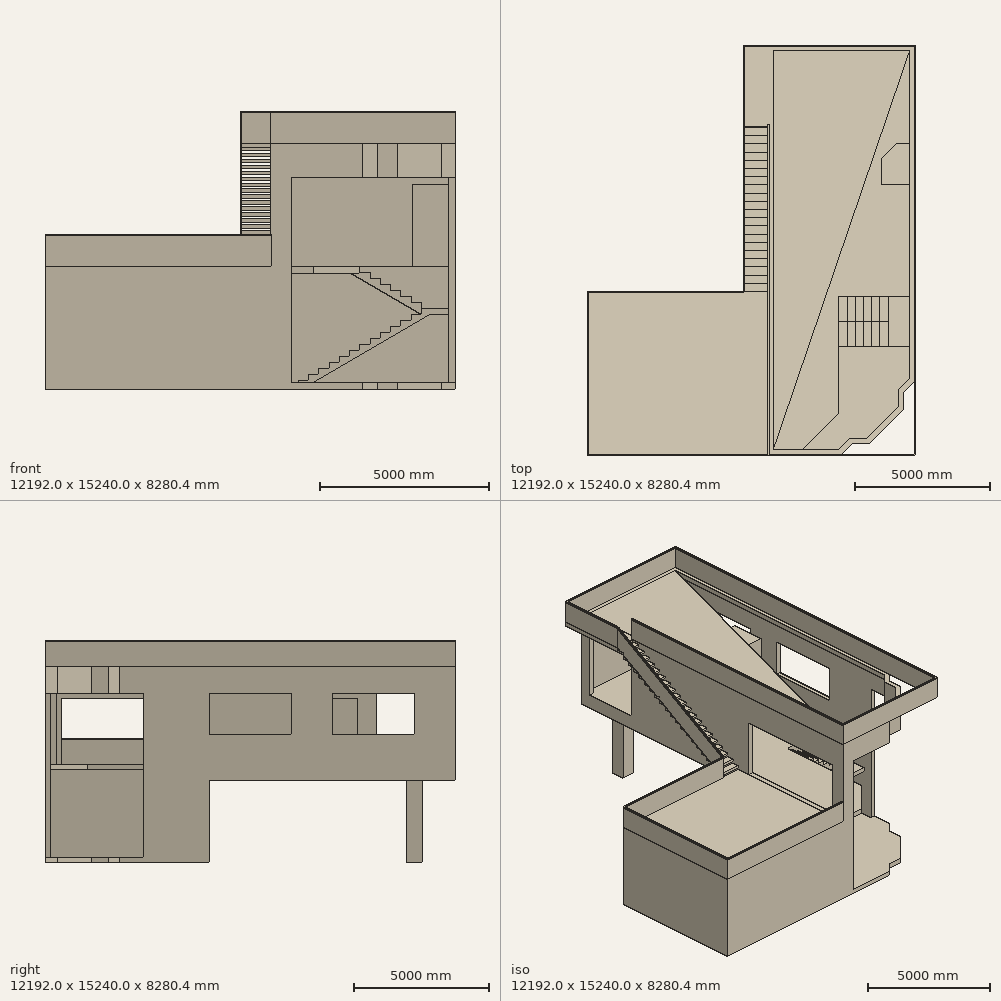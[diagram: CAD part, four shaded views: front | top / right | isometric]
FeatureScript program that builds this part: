
annotation { "Feature Type Name" : "Feature", "Feature Type Description" : "" }
export const myFeature = defineFeature(function(context is Context, id is Id, definition is map)
    precondition{}
    {
        {
            var Q0;
            Q0=qCreatedBy(makeId("Top.planeOp"),FACE);
            var sketch = newSketch(context, id + "F0", { "sketchPlane" : qUnion([Q0])});
            skLineSegment(sketch, "E0.bottom", {"start": v(0, 6096) * mm, "end": v(-12192, 6096) * mm});
            skLineSegment(sketch, "E0.top", {"start": v(0, 0) * mm, "end": v(-12192, 0) * mm});
            skLineSegment(sketch, "E0.left", {"start": v(0, 6096) * mm, "end": v(0, 0) * mm});
            skLineSegment(sketch, "E0.right", {"start": v(-12192, 6096) * mm, "end": v(-12192, 0) * mm});
            skSolve(sketch);
        }
        {
            var Q0;
            Q0 = qSketchRegion(id + "F0", true);
            extrude(context, id + "F1", {"entities" : qUnion([Q0]), "depth" : 3657.6 * mm, "offsetDistance" : 25.4 * mm});
        }
        {
            var Q0;
            Q0=makeQuery(id+"F1.opExtrude","CAP_FACE",FACE,{"disambiguationData":[OSD([sQuery(id+"F0.wireOp",EDGE,"E0.bottom"),sQuery(id+"F0.wireOp",EDGE,"E0.top"),sQuery(id+"F0.wireOp",EDGE,"E0.left"),sQuery(id+"F0.wireOp",EDGE,"E0.right")])],"isStart":false});
            var sketch = newSketch(context, id + "F2", { "sketchPlane" : qUnion([Q0])});
            skLineSegment(sketch, "E1", {"start": v(0, 6096) * mm, "end": v(0, 15240) * mm});
            skLineSegment(sketch, "E2", {"start": v(0, 15240) * mm, "end": v(-5486.4, 15240) * mm});
            skLineSegment(sketch, "E3", {"start": v(-5486.4, 15240) * mm, "end": v(-5486.4, 0) * mm});
            skLineSegment(sketch, "E4", {"start": v(-5486.4, 0) * mm, "end": v(0, 0) * mm});
            skLineSegment(sketch, "E5", {"start": v(0, 0) * mm, "end": v(0, 6096) * mm});
            skSolve(sketch);
        }
        {
            var Q0;
            {var subQ0=sQuery(id+"F2.wireOp",EDGE,"E1");Q0=makeQuery(id+"F2.imprint","IMPRINT",FACE,{"disambiguationData":[TD([[makeQuery(id+"F2.imprint","IMPRINT",EDGE,{"derivedFrom":subQ0}),1.0]])]});}
            var Q1;
            {var subQ0=sQuery(id+"F2.wireOp",EDGE,"E4");Q1=makeQuery(id+"F2.imprint","IMPRINT",FACE,{"disambiguationData":[TD([[makeQuery(id+"F2.imprint","IMPRINT",EDGE,{"derivedFrom":subQ0}),-1.0]])]});}
            extrude(context, id + "F3", {"entities" : qUnion([Q0, Q1]), "operationType" : NewBodyOperationType.ADD, "depth" : 3657.6 * mm, "offsetDistance" : 25.4 * mm});
        }
        {
            var Q0;
            Q0=makeQuery(id+"F3.opExtrude","SWEPT_FACE",FACE,{"disambiguationData":[OSD([sQuery(id+"F2.wireOp",EDGE,"E3")])]});
            var sketch = newSketch(context, id + "F4", { "sketchPlane" : qUnion([Q0])});
            skLineSegment(sketch, "E6.bottom", {"start": v(-6096, 3835.4) * mm, "end": v(-6400.8, 3835.4) * mm});
            skLineSegment(sketch, "E6.top", {"start": v(-6096, 3733.8) * mm, "end": v(-6400.8, 3733.8) * mm});
            skLineSegment(sketch, "E6.left", {"start": v(-6096, 3835.4) * mm, "end": v(-6096, 3733.8) * mm});
            skLineSegment(sketch, "E7", {"start": v(-6400.8, 3835.4) * mm, "end": v(-6400.8, 3733.8) * mm});
            skLineSegment(sketch, "E8", {"start": v(-6096, 3657.6) * mm, "end": v(-6096, 3733.8) * mm, "construction": true});
            skLineSegment(sketch, "E9", {"start": v(-6400.8, 3835.4) * mm, "end": v(-6096, 3657.6) * mm, "construction": true});
            skLineSegment(sketch, "E10", {"start": v(-6400.8, 3835.4) * mm, "end": v(-6705.6, 4013.2) * mm, "construction": true});
            skLineSegment(sketch, "E11.0.1.0", {"start": v(-6400.8, 4013.2) * mm, "end": v(-6705.6, 4013.2) * mm});
            skLineSegment(sketch, "E11.0.1.1", {"start": v(-6400.8, 3911.6) * mm, "end": v(-6705.6, 3911.6) * mm});
            skLineSegment(sketch, "E11.0.1.2", {"start": v(-6705.6, 4013.2) * mm, "end": v(-6705.6, 3911.6) * mm});
            skLineSegment(sketch, "E11.0.1.3", {"start": v(-6400.8, 4013.2) * mm, "end": v(-6400.8, 3911.6) * mm});
            skLineSegment(sketch, "E11.0.2.0", {"start": v(-6705.6, 4191) * mm, "end": v(-7010.4, 4191) * mm});
            skLineSegment(sketch, "E11.0.2.1", {"start": v(-6705.6, 4089.4) * mm, "end": v(-7010.4, 4089.4) * mm});
            skLineSegment(sketch, "E11.0.2.2", {"start": v(-7010.4, 4191) * mm, "end": v(-7010.4, 4089.4) * mm});
            skLineSegment(sketch, "E11.0.2.3", {"start": v(-6705.6, 4191) * mm, "end": v(-6705.6, 4089.4) * mm});
            skLineSegment(sketch, "E11.0.3.0", {"start": v(-7010.4, 4368.8) * mm, "end": v(-7315.2, 4368.8) * mm});
            skLineSegment(sketch, "E11.0.3.1", {"start": v(-7010.4, 4267.2) * mm, "end": v(-7315.2, 4267.2) * mm});
            skLineSegment(sketch, "E11.0.3.2", {"start": v(-7315.2, 4368.8) * mm, "end": v(-7315.2, 4267.2) * mm});
            skLineSegment(sketch, "E11.0.3.3", {"start": v(-7010.4, 4368.8) * mm, "end": v(-7010.4, 4267.2) * mm});
            skLineSegment(sketch, "E11.0.4.0", {"start": v(-7315.2, 4546.6) * mm, "end": v(-7620, 4546.6) * mm});
            skLineSegment(sketch, "E11.0.4.1", {"start": v(-7315.2, 4445) * mm, "end": v(-7620, 4445) * mm});
            skLineSegment(sketch, "E11.0.4.2", {"start": v(-7620, 4546.6) * mm, "end": v(-7620, 4445) * mm});
            skLineSegment(sketch, "E11.0.4.3", {"start": v(-7315.2, 4546.6) * mm, "end": v(-7315.2, 4445) * mm});
            skLineSegment(sketch, "E11.0.5.0", {"start": v(-7620, 4724.4) * mm, "end": v(-7924.8, 4724.4) * mm});
            skLineSegment(sketch, "E11.0.5.1", {"start": v(-7620, 4622.8) * mm, "end": v(-7924.8, 4622.8) * mm});
            skLineSegment(sketch, "E11.0.5.2", {"start": v(-7924.8, 4724.4) * mm, "end": v(-7924.8, 4622.8) * mm});
            skLineSegment(sketch, "E11.0.5.3", {"start": v(-7620, 4724.4) * mm, "end": v(-7620, 4622.8) * mm});
            skLineSegment(sketch, "E11.0.6.0", {"start": v(-7924.8, 4902.2) * mm, "end": v(-8229.6, 4902.2) * mm});
            skLineSegment(sketch, "E11.0.6.1", {"start": v(-7924.8, 4800.6) * mm, "end": v(-8229.6, 4800.6) * mm});
            skLineSegment(sketch, "E11.0.6.2", {"start": v(-8229.6, 4902.2) * mm, "end": v(-8229.6, 4800.6) * mm});
            skLineSegment(sketch, "E11.0.6.3", {"start": v(-7924.8, 4902.2) * mm, "end": v(-7924.8, 4800.6) * mm});
            skLineSegment(sketch, "E11.0.7.0", {"start": v(-8229.6, 5080) * mm, "end": v(-8534.4, 5080) * mm});
            skLineSegment(sketch, "E11.0.7.1", {"start": v(-8229.6, 4978.4) * mm, "end": v(-8534.4, 4978.4) * mm});
            skLineSegment(sketch, "E11.0.7.2", {"start": v(-8534.4, 5080) * mm, "end": v(-8534.4, 4978.4) * mm});
            skLineSegment(sketch, "E11.0.7.3", {"start": v(-8229.6, 5080) * mm, "end": v(-8229.6, 4978.4) * mm});
            skLineSegment(sketch, "E11.0.8.0", {"start": v(-8534.4, 5257.8) * mm, "end": v(-8839.2, 5257.8) * mm});
            skLineSegment(sketch, "E11.0.8.1", {"start": v(-8534.4, 5156.2) * mm, "end": v(-8839.2, 5156.2) * mm});
            skLineSegment(sketch, "E11.0.8.2", {"start": v(-8839.2, 5257.8) * mm, "end": v(-8839.2, 5156.2) * mm});
            skLineSegment(sketch, "E11.0.8.3", {"start": v(-8534.4, 5257.8) * mm, "end": v(-8534.4, 5156.2) * mm});
            skLineSegment(sketch, "E11.0.9.0", {"start": v(-8839.2, 5435.6) * mm, "end": v(-9144, 5435.6) * mm});
            skLineSegment(sketch, "E11.0.9.1", {"start": v(-8839.2, 5334) * mm, "end": v(-9144, 5334) * mm});
            skLineSegment(sketch, "E11.0.9.2", {"start": v(-9144, 5435.6) * mm, "end": v(-9144, 5334) * mm});
            skLineSegment(sketch, "E11.0.9.3", {"start": v(-8839.2, 5435.6) * mm, "end": v(-8839.2, 5334) * mm});
            skLineSegment(sketch, "E11.0.10.0", {"start": v(-9144, 5613.4) * mm, "end": v(-9448.8, 5613.4) * mm});
            skLineSegment(sketch, "E11.0.10.1", {"start": v(-9144, 5511.8) * mm, "end": v(-9448.8, 5511.8) * mm});
            skLineSegment(sketch, "E11.0.10.2", {"start": v(-9448.8, 5613.4) * mm, "end": v(-9448.8, 5511.8) * mm});
            skLineSegment(sketch, "E11.0.10.3", {"start": v(-9144, 5613.4) * mm, "end": v(-9144, 5511.8) * mm});
            skLineSegment(sketch, "E11.0.11.0", {"start": v(-9448.8, 5791.2) * mm, "end": v(-9753.6, 5791.2) * mm});
            skLineSegment(sketch, "E11.0.11.1", {"start": v(-9448.8, 5689.6) * mm, "end": v(-9753.6, 5689.6) * mm});
            skLineSegment(sketch, "E11.0.11.2", {"start": v(-9753.6, 5791.2) * mm, "end": v(-9753.6, 5689.6) * mm});
            skLineSegment(sketch, "E11.0.11.3", {"start": v(-9448.8, 5791.2) * mm, "end": v(-9448.8, 5689.6) * mm});
            skLineSegment(sketch, "E11.0.12.0", {"start": v(-9753.6, 5969) * mm, "end": v(-10058.4, 5969) * mm});
            skLineSegment(sketch, "E11.0.12.1", {"start": v(-9753.6, 5867.4) * mm, "end": v(-10058.4, 5867.4) * mm});
            skLineSegment(sketch, "E11.0.12.2", {"start": v(-10058.4, 5969) * mm, "end": v(-10058.4, 5867.4) * mm});
            skLineSegment(sketch, "E11.0.12.3", {"start": v(-9753.6, 5969) * mm, "end": v(-9753.6, 5867.4) * mm});
            skLineSegment(sketch, "E11.0.13.0", {"start": v(-10058.4, 6146.8) * mm, "end": v(-10363.2, 6146.8) * mm});
            skLineSegment(sketch, "E11.0.13.1", {"start": v(-10058.4, 6045.2) * mm, "end": v(-10363.2, 6045.2) * mm});
            skLineSegment(sketch, "E11.0.13.2", {"start": v(-10363.2, 6146.8) * mm, "end": v(-10363.2, 6045.2) * mm});
            skLineSegment(sketch, "E11.0.13.3", {"start": v(-10058.4, 6146.8) * mm, "end": v(-10058.4, 6045.2) * mm});
            skLineSegment(sketch, "E11.0.14.0", {"start": v(-10363.2, 6324.6) * mm, "end": v(-10668, 6324.6) * mm});
            skLineSegment(sketch, "E11.0.14.1", {"start": v(-10363.2, 6223) * mm, "end": v(-10668, 6223) * mm});
            skLineSegment(sketch, "E11.0.14.2", {"start": v(-10668, 6324.6) * mm, "end": v(-10668, 6223) * mm});
            skLineSegment(sketch, "E11.0.14.3", {"start": v(-10363.2, 6324.6) * mm, "end": v(-10363.2, 6223) * mm});
            skLineSegment(sketch, "E11.0.15.0", {"start": v(-10668, 6502.4) * mm, "end": v(-10972.8, 6502.4) * mm});
            skLineSegment(sketch, "E11.0.15.1", {"start": v(-10668, 6400.8) * mm, "end": v(-10972.8, 6400.8) * mm});
            skLineSegment(sketch, "E11.0.15.2", {"start": v(-10972.8, 6502.4) * mm, "end": v(-10972.8, 6400.8) * mm});
            skLineSegment(sketch, "E11.0.15.3", {"start": v(-10668, 6502.4) * mm, "end": v(-10668, 6400.8) * mm});
            skLineSegment(sketch, "E11.0.16.0", {"start": v(-10972.8, 6680.2) * mm, "end": v(-11277.6, 6680.2) * mm});
            skLineSegment(sketch, "E11.0.16.1", {"start": v(-10972.8, 6578.6) * mm, "end": v(-11277.6, 6578.6) * mm});
            skLineSegment(sketch, "E11.0.16.2", {"start": v(-11277.6, 6680.2) * mm, "end": v(-11277.6, 6578.6) * mm});
            skLineSegment(sketch, "E11.0.16.3", {"start": v(-10972.8, 6680.2) * mm, "end": v(-10972.8, 6578.6) * mm});
            skLineSegment(sketch, "E11.0.17.0", {"start": v(-11277.6, 6858) * mm, "end": v(-11582.4, 6858) * mm});
            skLineSegment(sketch, "E11.0.17.1", {"start": v(-11277.6, 6756.4) * mm, "end": v(-11582.4, 6756.4) * mm});
            skLineSegment(sketch, "E11.0.17.2", {"start": v(-11582.4, 6858) * mm, "end": v(-11582.4, 6756.4) * mm});
            skLineSegment(sketch, "E11.0.17.3", {"start": v(-11277.6, 6858) * mm, "end": v(-11277.6, 6756.4) * mm});
            skLineSegment(sketch, "E11.0.18.0", {"start": v(-11582.4, 7035.8) * mm, "end": v(-11887.2, 7035.8) * mm});
            skLineSegment(sketch, "E11.0.18.1", {"start": v(-11582.4, 6934.2) * mm, "end": v(-11887.2, 6934.2) * mm});
            skLineSegment(sketch, "E11.0.18.2", {"start": v(-11887.2, 7035.8) * mm, "end": v(-11887.2, 6934.2) * mm});
            skLineSegment(sketch, "E11.0.18.3", {"start": v(-11582.4, 7035.8) * mm, "end": v(-11582.4, 6934.2) * mm});
            skLineSegment(sketch, "E11.0.19.0", {"start": v(-11887.2, 7213.6) * mm, "end": v(-12192, 7213.6) * mm});
            skLineSegment(sketch, "E11.0.19.1", {"start": v(-11887.2, 7112) * mm, "end": v(-12192, 7112) * mm});
            skLineSegment(sketch, "E11.0.19.2", {"start": v(-12192, 7213.6) * mm, "end": v(-12192, 7112) * mm});
            skLineSegment(sketch, "E11.0.19.3", {"start": v(-11887.2, 7213.6) * mm, "end": v(-11887.2, 7112) * mm});
            skLineSegment(sketch, "E11.direction1", {"start": v(-6400.8, 3733.8) * mm, "end": v(-6375.4, 3733.8) * mm, "construction": true});
            skLineSegment(sketch, "E11.direction2", {"start": v(-6400.8, 3733.8) * mm, "end": v(-6705.6, 3911.6) * mm, "construction": true});
            skLineSegment(sketch, "E12", {"start": v(-15240, 7112) * mm, "end": v(-15240, 7315.2) * mm});
            skLineSegment(sketch, "E13", {"start": v(-12242.8, 7315.2) * mm, "end": v(-12242.8, 7112) * mm});
            skLineSegment(sketch, "E14", {"start": v(-12242.8, 7112) * mm, "end": v(-15240, 7112) * mm});
            skLineSegment(sketch, "E15", {"start": v(-15240, 7315.2) * mm, "end": v(-12242.8, 7315.2) * mm});
            skSolve(sketch);
        }
        {
            var Q0;
            Q0 = qSketchRegion(id + "F4", true);
            extrude(context, id + "F5", {"entities" : qUnion([Q0]), "operationType" : NewBodyOperationType.ADD, "depth" : 914.4 * mm, "offsetDistance" : 25.4 * mm});
        }
        {
            var Q0;
            Q0=makeQuery(id+"F1.opExtrude","CAP_FACE",FACE,{"disambiguationData":[OSD([sQuery(id+"F0.wireOp",EDGE,"E0.bottom"),sQuery(id+"F0.wireOp",EDGE,"E0.top"),sQuery(id+"F0.wireOp",EDGE,"E0.left"),sQuery(id+"F0.wireOp",EDGE,"E0.right")])],"isStart":false});
            var sketch = newSketch(context, id + "F6", { "sketchPlane" : qUnion([Q0])});
            skLineSegment(sketch, "E16.0", {"start": v(-5486.4, 50.8) * mm, "end": v(-12141.2, 50.8) * mm});
            skLineSegment(sketch, "E16.1", {"start": v(-12141.2, 6045.2) * mm, "end": v(-12141.2, 50.8) * mm});
            skLineSegment(sketch, "E16.2", {"start": v(-6400.8, 6045.2) * mm, "end": v(-12141.2, 6045.2) * mm});
            skLineSegment(sketch, "E17", {"start": v(-5486.4, 50.8) * mm, "end": v(-5486.4, 0) * mm});
            skLineSegment(sketch, "E18", {"start": v(-5486.4, 0) * mm, "end": v(-12192, 0) * mm});
            skLineSegment(sketch, "E19", {"start": v(-12192, 0) * mm, "end": v(-12192, 6096) * mm});
            skLineSegment(sketch, "E20", {"start": v(-12192, 6096) * mm, "end": v(-6400.8, 6096) * mm});
            skLineSegment(sketch, "E21", {"start": v(-6400.8, 6096) * mm, "end": v(-6400.8, 6045.2) * mm});
            skSolve(sketch);
        }
        {
            var Q0;
            Q0=makeQuery(id+"F6.imprint","IMPRINT",FACE,{"disambiguationData":[TD([[makeQuery(id+"F6.imprint","IMPRINT",EDGE,{"derivedFrom":sQuery(id+"F6.wireOp",EDGE,"E16.0")}),1.0]])]});
            extrude(context, id + "F7", {"entities" : qUnion([Q0]), "depth" : 914.4 * mm, "offsetDistance" : 25.4 * mm});
        }
        {
            var Q0;
            Q0=makeQuery(id+"F7.opExtrude","CAP_FACE",FACE,{"disambiguationData":[OSD([sQuery(id+"F6.wireOp",EDGE,"E16.0"),sQuery(id+"F6.wireOp",EDGE,"E16.1"),sQuery(id+"F6.wireOp",EDGE,"E16.2"),sQuery(id+"F6.wireOp",EDGE,"E17"),sQuery(id+"F6.wireOp",EDGE,"E18"),sQuery(id+"F6.wireOp",EDGE,"E19"),sQuery(id+"F6.wireOp",EDGE,"E20"),sQuery(id+"F6.wireOp",EDGE,"E21")])],"isStart":false});
            extrude(context, id + "F8", {"entities" : qUnion([Q0]), "depth" : 50.8 * mm, "offsetDistance" : 25.4 * mm});
        }
        {
            var Q0;
            Q0=makeQuery(id+"F5.boolean.opBoolean","MERGE",FACE,{"derivedFrom":[makeQuery(id+"F3.opExtrude","CAP_FACE",FACE,{"disambiguationData":[OSD([sQuery(id+"F2.wireOp",EDGE,"E1"),sQuery(id+"F2.wireOp",EDGE,"E2"),sQuery(id+"F2.wireOp",EDGE,"E3"),sQuery(id+"F2.wireOp",EDGE,"E4"),sQuery(id+"F2.wireOp",EDGE,"E5")])],"isStart":false}),makeQuery(id+"F5.opExtrude","SWEPT_FACE",FACE,{"disambiguationData":[OSD([sQuery(id+"F4.wireOp",EDGE,"E15")])]})]});
            var sketch = newSketch(context, id + "F9", { "sketchPlane" : qUnion([Q0])});
            skLineSegment(sketch, "E22.0", {"start": v(-50.8, 50.8) * mm, "end": v(-50.8, 15189.2) * mm});
            skLineSegment(sketch, "E22.1", {"start": v(-6350, 15189.2) * mm, "end": v(-6350, 12293.6) * mm});
            skLineSegment(sketch, "E22.2", {"start": v(-5486.4, 12293.6) * mm, "end": v(-5435.6, 12293.6) * mm});
            skLineSegment(sketch, "E22.3", {"start": v(-50.8, 15189.2) * mm, "end": v(-6350, 15189.2) * mm});
            skLineSegment(sketch, "E22.4", {"start": v(-5435.6, 12293.6) * mm, "end": v(-5435.6, 50.8) * mm});
            skLineSegment(sketch, "E22.5", {"start": v(-5435.6, 50.8) * mm, "end": v(-50.8, 50.8) * mm});
            skLineSegment(sketch, "E23", {"start": v(-6400.8, 12242.8) * mm, "end": v(-6400.8, 15240) * mm});
            skLineSegment(sketch, "E24", {"start": v(-6400.8, 15240) * mm, "end": v(0, 15240) * mm});
            skLineSegment(sketch, "E25", {"start": v(0, 15240) * mm, "end": v(0, 0) * mm});
            skLineSegment(sketch, "E26", {"start": v(0, 0) * mm, "end": v(-5486.4, 0) * mm});
            skLineSegment(sketch, "E27", {"start": v(-5486.4, 0) * mm, "end": v(-5486.4, 12293.6) * mm});
            skLineSegment(sketch, "E28", {"start": v(-6350, 12293.6) * mm, "end": v(-6350, 12242.8) * mm});
            skSolve(sketch);
        }
        {
            var Q0;
            Q0=makeQuery(id+"F9.imprint","IMPRINT",FACE,{"disambiguationData":[TD([[makeQuery(id+"F9.imprint","IMPRINT",EDGE,{"derivedFrom":sQuery(id+"F9.wireOp",EDGE,"E22.0")}),-1.0]])]});
            extrude(context, id + "F10", {"entities" : qUnion([Q0]), "depth" : 914.4 * mm, "offsetDistance" : 25.4 * mm});
        }
        {
            var Q0;
            Q0=makeQuery(id+"F10.opExtrude","CAP_FACE",FACE,{"disambiguationData":[OSD([sQuery(id+"F2.wireOp",EDGE,"E3"),sQuery(id+"F4.wireOp",EDGE,"E13"),sQuery(id+"F4.wireOp",EDGE,"E15"),sQuery(id+"F9.wireOp",EDGE,"E22.0"),sQuery(id+"F9.wireOp",EDGE,"E22.1"),sQuery(id+"F9.wireOp",EDGE,"E22.2"),sQuery(id+"F9.wireOp",EDGE,"E22.3"),sQuery(id+"F9.wireOp",EDGE,"E22.4"),sQuery(id+"F9.wireOp",EDGE,"E22.5"),sQuery(id+"F9.wireOp",EDGE,"E23"),sQuery(id+"F9.wireOp",EDGE,"E24"),sQuery(id+"F9.wireOp",EDGE,"E25"),sQuery(id+"F9.wireOp",EDGE,"E26"),sQuery(id+"F9.wireOp",EDGE,"E27"),sQuery(id+"F9.wireOp",EDGE,"E28")])],"isStart":false});
            extrude(context, id + "F11", {"entities" : qUnion([Q0]), "depth" : 50.8 * mm, "offsetDistance" : 25.4 * mm});
        }
        {
            var Q0;
            Q0=makeQuery(id+"F5.opExtrude","CAP_FACE",FACE,{"disambiguationData":[OSD([sQuery(id+"F4.wireOp",EDGE,"E11.0.19.0"),sQuery(id+"F4.wireOp",EDGE,"E11.0.19.1"),sQuery(id+"F4.wireOp",EDGE,"E11.0.19.2"),sQuery(id+"F4.wireOp",EDGE,"E11.0.19.3")])],"isStart":false});
            var sketch = newSketch(context, id + "F12", { "sketchPlane" : qUnion([Q0])});
            skLineSegment(sketch, "E29", {"start": v(-6096, 3657.6) * mm, "end": v(-12242.8, 7315.2) * mm});
            skLineSegment(sketch, "E30", {"start": v(-12242.8, 7315.2) * mm, "end": v(-12242.8, 8229.6) * mm});
            skLineSegment(sketch, "E31", {"start": v(-12242.8, 8229.6) * mm, "end": v(-6096, 4572) * mm});
            skLineSegment(sketch, "E32", {"start": v(-6096, 4572) * mm, "end": v(-6096, 3657.6) * mm});
            skSolve(sketch);
        }
        {
            var Q0;
            {var subQ0=sQuery(id+"F12.wireOp",EDGE,"E30");Q0=makeQuery(id+"F12.imprint","IMPRINT",FACE,{"disambiguationData":[TD([[makeQuery(id+"F12.imprint","IMPRINT",EDGE,{"derivedFrom":subQ0}),-1.0]])]});}
            extrude(context, id + "F13", {"entities" : qUnion([Q0]), "oppositeDirection" : true, "depth" : 50.8 * mm, "offsetDistance" : 25.4 * mm});
        }
        {
            var Q0;
            Q0=makeQuery(id+"F3.opExtrude","SWEPT_FACE",FACE,{"disambiguationData":[OSD([sQuery(id+"F2.wireOp",EDGE,"E3")])]});
            var sketch = newSketch(context, id + "F14", { "sketchPlane" : qUnion([Q0])});
            skLineSegment(sketch, "E33", {"start": v(-5486.4, 3657.6) * mm, "end": v(-5486.4, 6096) * mm});
            skLineSegment(sketch, "E34", {"start": v(-5486.4, 6096) * mm, "end": v(-609.6, 6096) * mm});
            skLineSegment(sketch, "E35", {"start": v(-609.6, 6096) * mm, "end": v(-609.6, 3657.6) * mm});
            skLineSegment(sketch, "E36", {"start": v(-3048, 6096) * mm, "end": v(-3048, 3657.6) * mm, "construction": true});
            skSolve(sketch);
        }
        {
            var Q0;
            {var subQ0=sQuery(id+"F14.wireOp",EDGE,"E33");Q0=makeQuery(id+"F14.imprint","IMPRINT",FACE,{"disambiguationData":[TD([[makeQuery(id+"F14.imprint","IMPRINT",EDGE,{"derivedFrom":subQ0}),-1.0]])]});}
            extrude(context, id + "F15", {"entities" : qUnion([Q0]), "operationType" : NewBodyOperationType.REMOVE, "oppositeDirection" : true, "depth" : 228.6 * mm, "offsetDistance" : 25.4 * mm});
        }
        {
            var Q0;
            Q0=makeQuery(id+"F15.boolean.opBoolean","COPY",FACE,{"derivedFrom":makeQuery(id+"F15.opExtrude","CAP_FACE",FACE,{"disambiguationData":[OSD([sQuery(id+"F2.wireOp",EDGE,"E3"),sQuery(id+"F14.wireOp",EDGE,"E33"),sQuery(id+"F14.wireOp",EDGE,"E34"),sQuery(id+"F14.wireOp",EDGE,"E35")])],"isStart":false})});
            shell(context, id + "F16", {"entities" : qUnion([Q0]), "thickness" : 203.2 * mm});
        }
        {
            var Q0;
            Q0=makeQuery(id+"F3.boolean.opBoolean","MERGE",FACE,{"derivedFrom":[makeQuery(id+"F1.opExtrude","SWEPT_FACE",FACE,{"disambiguationData":[OSD([sQuery(id+"F0.wireOp",EDGE,"E0.left")])]}),makeQuery(id+"F3.opExtrude","SWEPT_FACE",FACE,{"disambiguationData":[OSD([sQuery(id+"F2.wireOp",EDGE,"E1"),sQuery(id+"F2.wireOp",EDGE,"E5")])]})]});
            var sketch = newSketch(context, id + "F17", { "sketchPlane" : qUnion([Q0])});
            skLineSegment(sketch, "E37.bottom", {"start": v(0, 6299.2) * mm, "end": v(3657.6, 6299.2) * mm});
            skLineSegment(sketch, "E37.top", {"start": v(0, 203.2) * mm, "end": v(3657.6, 203.2) * mm});
            skLineSegment(sketch, "E37.left", {"start": v(0, 6299.2) * mm, "end": v(0, 203.2) * mm});
            skLineSegment(sketch, "E37.right", {"start": v(3657.6, 6299.2) * mm, "end": v(3657.6, 203.2) * mm});
            skSolve(sketch);
        }
        {
            var Q0;
            Q0=makeQuery(id+"F17.imprint","IMPRINT",FACE,{"disambiguationData":[TD([[makeQuery(id+"F17.imprint","IMPRINT",EDGE,{"derivedFrom":sQuery(id+"F17.wireOp",EDGE,"E37.bottom")}),-1.0]])]});
            extrude(context, id + "F18", {"entities" : qUnion([Q0]), "operationType" : NewBodyOperationType.REMOVE, "oppositeDirection" : true, "depth" : 4876.8 * mm, "offsetDistance" : 25.4 * mm});
        }
        {
            var Q0;
            Q0=makeQuery(id+"F3.boolean.opBoolean","MERGE",FACE,{"derivedFrom":[makeQuery(id+"F1.opExtrude","SWEPT_FACE",FACE,{"disambiguationData":[OSD([sQuery(id+"F0.wireOp",EDGE,"E0.left")])]}),makeQuery(id+"F3.opExtrude","SWEPT_FACE",FACE,{"disambiguationData":[OSD([sQuery(id+"F2.wireOp",EDGE,"E1"),sQuery(id+"F2.wireOp",EDGE,"E5")])]})]});
            var sketch = newSketch(context, id + "F19", { "sketchPlane" : qUnion([Q0])});
            skLineSegment(sketch, "E38.bottom", {"start": v(6096, 6299.2) * mm, "end": v(9144, 6299.2) * mm});
            skLineSegment(sketch, "E38.top", {"start": v(6096, 4775.2) * mm, "end": v(9144, 4775.2) * mm});
            skLineSegment(sketch, "E38.left", {"start": v(6096, 6299.2) * mm, "end": v(6096, 4775.2) * mm});
            skLineSegment(sketch, "E38.right", {"start": v(9144, 6299.2) * mm, "end": v(9144, 4775.2) * mm});
            skLineSegment(sketch, "E39.bottom", {"start": v(10668, 6299.2) * mm, "end": v(13716, 6299.2) * mm});
            skLineSegment(sketch, "E39.top", {"start": v(10668, 4775.2) * mm, "end": v(13716, 4775.2) * mm});
            skLineSegment(sketch, "E39.left", {"start": v(10668, 6299.2) * mm, "end": v(10668, 4775.2) * mm});
            skLineSegment(sketch, "E39.right", {"start": v(13716, 6299.2) * mm, "end": v(13716, 4775.2) * mm});
            skSolve(sketch);
        }
        {
            var Q0;
            Q0=makeQuery(id+"F19.imprint","IMPRINT",FACE,{"disambiguationData":[TD([[makeQuery(id+"F19.imprint","IMPRINT",EDGE,{"derivedFrom":sQuery(id+"F19.wireOp",EDGE,"E38.bottom")}),-1.0]])]});
            var Q1;
            Q1=makeQuery(id+"F19.imprint","IMPRINT",FACE,{"disambiguationData":[TD([[makeQuery(id+"F19.imprint","IMPRINT",EDGE,{"derivedFrom":sQuery(id+"F19.wireOp",EDGE,"E39.bottom")}),-1.0]])]});
            extrude(context, id + "F20", {"entities" : qUnion([Q0, Q1]), "operationType" : NewBodyOperationType.REMOVE, "endBound" : BoundingType.UP_TO_NEXT, "oppositeDirection" : true, "depth" : 25.4 * mm, "offsetDistance" : 25.4 * mm});
        }
        {
            var Q0;
            Q0=makeQuery(id+"F3.opExtrude","CAP_FACE",FACE,{"disambiguationData":[OSD([sQuery(id+"F2.wireOp",EDGE,"E1"),sQuery(id+"F2.wireOp",EDGE,"E2"),sQuery(id+"F2.wireOp",EDGE,"E3"),sQuery(id+"F2.wireOp",EDGE,"E4"),sQuery(id+"F2.wireOp",EDGE,"E5")])],"isStart":true});
            extrude(context, id + "F21", {"entities" : qUnion([Q0]), "operationType" : NewBodyOperationType.ADD, "depth" : 609.6 * mm, "offsetDistance" : 25.4 * mm});
        }
        {
            var Q0;
            Q0=makeQuery(id+"F16.opShell","OFFSET_FACE",FACE,{"disambiguationData":[OSD([sQuery(id+"F2.wireOp",EDGE,"E1"),sQuery(id+"F2.wireOp",EDGE,"E2"),sQuery(id+"F2.wireOp",EDGE,"E3"),sQuery(id+"F2.wireOp",EDGE,"E4"),sQuery(id+"F2.wireOp",EDGE,"E5")])]});
            extrude(context, id + "F22", {"entities" : qUnion([Q0]), "operationType" : NewBodyOperationType.REMOVE, "oppositeDirection" : true, "depth" : 203.2 * mm, "offsetDistance" : 25.4 * mm});
        }
        {
            var Q0;
            Q0=makeQuery(id+"F22.boolean.opBoolean","COPY",FACE,{"derivedFrom":makeQuery(id+"F22.opExtrude","CAP_FACE",FACE,{"disambiguationData":[OSD([sQuery(id+"F2.wireOp",EDGE,"E1"),sQuery(id+"F2.wireOp",EDGE,"E2"),sQuery(id+"F2.wireOp",EDGE,"E3"),sQuery(id+"F2.wireOp",EDGE,"E4"),sQuery(id+"F2.wireOp",EDGE,"E5")])],"isStart":false})});
            var sketch = newSketch(context, id + "F23", { "sketchPlane" : qUnion([Q0])});
            skLineSegment(sketch, "E40", {"start": v(-5283.2, 5892.8) * mm, "end": v(-5283.2, 203.2) * mm});
            skLineSegment(sketch, "E41", {"start": v(-5283.2, 203.2) * mm, "end": v(-4216.4, 203.2) * mm});
            skLineSegment(sketch, "E42", {"start": v(-4216.4, 203.2) * mm, "end": v(-2844.8, 1574.8) * mm});
            skLineSegment(sketch, "E43", {"start": v(-2844.8, 1574.8) * mm, "end": v(-2844.8, 5892.8) * mm});
            skLineSegment(sketch, "E44", {"start": v(-5283.2, 5892.8) * mm, "end": v(-2844.8, 5892.8) * mm});
            skSolve(sketch);
        }
        {
            var Q0;
            Q0=makeQuery(id+"F23.imprint","IMPRINT",FACE,{"disambiguationData":[TD([[makeQuery(id+"F23.imprint","IMPRINT",EDGE,{"derivedFrom":sQuery(id+"F23.wireOp",EDGE,"E40")}),1.0]])]});
            extrude(context, id + "F24", {"entities" : qUnion([Q0]), "operationType" : NewBodyOperationType.ADD, "oppositeDirection" : true, "depth" : 203.2 * mm, "offsetDistance" : 25.4 * mm});
        }
        {
            var Q0;
            {var subQ0=sQuery(id+"F0.wireOp",EDGE,"E0.right");var subQ1=sQuery(id+"F0.wireOp",EDGE,"E0.left");var subQ2=sQuery(id+"F0.wireOp",EDGE,"E0.top");var subQ3=sQuery(id+"F0.wireOp",EDGE,"E0.bottom");Q0=makeQuery(id+"F18.boolean.opBoolean","MERGE",FACE,{"derivedFrom":[makeQuery(id+"F16.opShell","OFFSET_FACE",FACE,{"disambiguationData":[OSD([subQ3,subQ2,subQ1,subQ0]),TDD([makeQuery(id+"F1.opExtrude","CAP_FACE",FACE,{"disambiguationData":[OSD([subQ3,subQ2,subQ1,subQ0])],"isStart":true})])]}),makeQuery(id+"F18.opExtrude","SWEPT_FACE",FACE,{"disambiguationData":[OSD([sQuery(id+"F17.wireOp",EDGE,"E37.top")])]})]});}
            var sketch = newSketch(context, id + "F25", { "sketchPlane" : qUnion([Q0])});
            skLineSegment(sketch, "E45", {"start": v(-4876.8, 0) * mm, "end": v(0, 0) * mm});
            skLineSegment(sketch, "E46", {"start": v(0, 0) * mm, "end": v(0, 3657.6) * mm});
            skLineSegment(sketch, "E47", {"start": v(0, 3657.6) * mm, "end": v(-101.6, 3657.6) * mm});
            skLineSegment(sketch, "E48", {"start": v(-101.6, 3657.6) * mm, "end": v(-101.6, 101.6) * mm});
            skLineSegment(sketch, "E49", {"start": v(-101.6, 101.6) * mm, "end": v(-4876.8, 101.6) * mm});
            skLineSegment(sketch, "E50", {"start": v(-4876.8, 101.6) * mm, "end": v(-4876.8, 0) * mm});
            skSolve(sketch);
        }
        {
            var Q0;
            Q0=makeQuery(id+"F21.opExtrude","CAP_FACE",FACE,{"disambiguationData":[OSD([sQuery(id+"F2.wireOp",EDGE,"E1"),sQuery(id+"F2.wireOp",EDGE,"E2"),sQuery(id+"F2.wireOp",EDGE,"E3"),sQuery(id+"F2.wireOp",EDGE,"E4"),sQuery(id+"F2.wireOp",EDGE,"E5")])],"isStart":false});
            var sketch = newSketch(context, id + "F26", { "sketchPlane" : qUnion([Q0])});
            skLineSegment(sketch, "E51.bottom", {"start": v(-609.6, -14020.8) * mm, "end": v(-1219.2, -14020.8) * mm});
            skLineSegment(sketch, "E51.top", {"start": v(-609.6, -13411.2) * mm, "end": v(-1219.2, -13411.2) * mm});
            skLineSegment(sketch, "E51.left", {"start": v(-609.6, -14020.8) * mm, "end": v(-609.6, -13411.2) * mm});
            skLineSegment(sketch, "E51.right", {"start": v(-1219.2, -14020.8) * mm, "end": v(-1219.2, -13411.2) * mm});
            skLineSegment(sketch, "E52.bottom", {"start": v(-4267.2, -13411.2) * mm, "end": v(-4876.8, -13411.2) * mm});
            skLineSegment(sketch, "E52.top", {"start": v(-4267.2, -14020.8) * mm, "end": v(-4876.8, -14020.8) * mm});
            skLineSegment(sketch, "E52.left", {"start": v(-4267.2, -13411.2) * mm, "end": v(-4267.2, -14020.8) * mm});
            skLineSegment(sketch, "E52.right", {"start": v(-4876.8, -13411.2) * mm, "end": v(-4876.8, -14020.8) * mm});
            skLineSegment(sketch, "E53", {"start": v(-609.6, -14020.8) * mm, "end": v(0, -14020.8) * mm, "construction": true});
            skLineSegment(sketch, "E54", {"start": v(-609.6, -15240) * mm, "end": v(-609.6, -14020.8) * mm, "construction": true});
            skLineSegment(sketch, "E55", {"start": v(-4876.8, -14020.8) * mm, "end": v(-5486.4, -14020.8) * mm, "construction": true});
            skLineSegment(sketch, "E56", {"start": v(-4876.8, -15240) * mm, "end": v(-4876.8, -14020.8) * mm, "construction": true});
            skSolve(sketch);
        }
        {
            var Q0;
            Q0=makeQuery(id+"F26.imprint","IMPRINT",FACE,{"disambiguationData":[TD([[makeQuery(id+"F26.imprint","IMPRINT",EDGE,{"derivedFrom":sQuery(id+"F26.wireOp",EDGE,"E51.bottom")}),-1.0]])]});
            var Q1;
            Q1=makeQuery(id+"F26.imprint","IMPRINT",FACE,{"disambiguationData":[TD([[makeQuery(id+"F26.imprint","IMPRINT",EDGE,{"derivedFrom":sQuery(id+"F26.wireOp",EDGE,"E52.bottom")}),1.0]])]});
            var Q2;
            Q2=makeQuery(id+"F1.opExtrude","CAP_FACE",FACE,{"disambiguationData":[OSD([sQuery(id+"F0.wireOp",EDGE,"E0.bottom"),sQuery(id+"F0.wireOp",EDGE,"E0.top"),sQuery(id+"F0.wireOp",EDGE,"E0.left"),sQuery(id+"F0.wireOp",EDGE,"E0.right")])],"isStart":true});
            extrude(context, id + "F27", {"entities" : qUnion([Q0, Q1]), "endBound" : BoundingType.UP_TO_SURFACE, "depth" : 25.4 * mm, "endBoundEntityFace" : qUnion([Q2]), "offsetDistance" : 25.4 * mm});
        }
        {
            var Q0;
            {var subQ0=sQuery(id+"F2.wireOp",EDGE,"E3");Q0=makeQuery(id+"F22.boolean.opBoolean","MERGE",FACE,{"derivedFrom":[makeQuery(id+"F16.opShell","OFFSET_FACE",FACE,{"disambiguationData":[OSD([subQ0])]}),makeQuery(id+"F22.opExtrude","SWEPT_FACE",FACE,{"disambiguationData":[OSD([subQ0])]})]});}
            var sketch = newSketch(context, id + "F28", { "sketchPlane" : qUnion([Q0])});
            skLineSegment(sketch, "E57.bottom", {"start": v(14732, 3657.6) * mm, "end": v(12293.6, 3657.6) * mm});
            skLineSegment(sketch, "E57.top", {"start": v(14732, 7112) * mm, "end": v(12293.6, 7112) * mm});
            skLineSegment(sketch, "E57.left", {"start": v(14732, 3657.6) * mm, "end": v(14732, 7112) * mm});
            skLineSegment(sketch, "E57.right", {"start": v(12293.6, 3657.6) * mm, "end": v(12293.6, 7112) * mm});
            skSolve(sketch);
        }
        {
            var Q0;
            Q0 = qSketchRegion(id + "F28", true);
            extrude(context, id + "F29", {"entities" : qUnion([Q0]), "operationType" : NewBodyOperationType.REMOVE, "endBound" : BoundingType.UP_TO_NEXT, "oppositeDirection" : true, "depth" : 25.4 * mm, "offsetDistance" : 25.4 * mm});
        }
        {
            var Q0;
            Q0=makeQuery(id+"F13.opExtrude","SWEPT_FACE",FACE,{"disambiguationData":[OSD([sQuery(id+"F12.wireOp",EDGE,"E31")])]});
            extrude(context, id + "F30", {"entities" : qUnion([Q0]), "depth" : 50.8 * mm, "offsetDistance" : 25.4 * mm});
        }
        {
            var Q0;
            {var subQ0=sQuery(id+"F2.wireOp",EDGE,"E3");Q0=makeQuery(id+"F29.boolean.opBoolean","MERGE",FACE,{"derivedFrom":[makeQuery(id+"F24.boolean.opBoolean","MERGE",FACE,{"derivedFrom":[makeQuery(id+"F15.boolean.opBoolean","MERGE",FACE,{"derivedFrom":[makeQuery(id+"F1.opExtrude","CAP_FACE",FACE,{"disambiguationData":[OSD([sQuery(id+"F0.wireOp",EDGE,"E0.bottom"),sQuery(id+"F0.wireOp",EDGE,"E0.top"),sQuery(id+"F0.wireOp",EDGE,"E0.left"),sQuery(id+"F0.wireOp",EDGE,"E0.right")])],"isStart":false}),makeQuery(id+"F15.opExtrude","SWEPT_FACE",FACE,{"disambiguationData":[OSD([subQ0])]})]}),makeQuery(id+"F22.boolean.opBoolean","COPY",FACE,{"derivedFrom":makeQuery(id+"F22.opExtrude","CAP_FACE",FACE,{"disambiguationData":[OSD([sQuery(id+"F2.wireOp",EDGE,"E1"),sQuery(id+"F2.wireOp",EDGE,"E2"),subQ0,sQuery(id+"F2.wireOp",EDGE,"E4"),sQuery(id+"F2.wireOp",EDGE,"E5")])],"isStart":false})}),makeQuery(id+"F24.opExtrude","CAP_FACE",FACE,{"disambiguationData":[OSD([sQuery(id+"F23.wireOp",EDGE,"E40"),sQuery(id+"F23.wireOp",EDGE,"E41"),sQuery(id+"F23.wireOp",EDGE,"E42"),sQuery(id+"F23.wireOp",EDGE,"zWNXu1ST-T9Qo-mUke-BK7y-AsgEIesGl4v7"),sQuery(id+"F23.wireOp",EDGE,"rUGLp6VW-P6g0-epgt-ylcF-GukmlLlvLHMA"),sQuery(id+"F23.wireOp",EDGE,"TF8LNKhQ-o0ex-5smu-12g6-qV7lk8wERiVb")])],"isStart":true})]}),makeQuery(id+"F29.opExtrude","SWEPT_FACE",FACE,{"disambiguationData":[OSD([sQuery(id+"F28.wireOp",EDGE,"E57.bottom")])]})]});}
            var sketch = newSketch(context, id + "F31", { "sketchPlane" : qUnion([Q0])});
            skLineSegment(sketch, "E58.bottom", {"start": v(-5486.4, 5486.4) * mm, "end": v(-5257.8, 5486.4) * mm});
            skLineSegment(sketch, "E58.top", {"start": v(-5486.4, 609.6) * mm, "end": v(-5257.8, 609.6) * mm});
            skLineSegment(sketch, "E58.left", {"start": v(-5486.4, 5486.4) * mm, "end": v(-5486.4, 609.6) * mm});
            skLineSegment(sketch, "E58.right", {"start": v(-5257.8, 5486.4) * mm, "end": v(-5257.8, 609.6) * mm});
            skSolve(sketch);
        }
        {
            var Q0;
            Q0=makeQuery(id+"F31.imprint","IMPRINT",FACE,{"disambiguationData":[TD([[makeQuery(id+"F31.imprint","IMPRINT",EDGE,{"derivedFrom":sQuery(id+"F31.wireOp",EDGE,"E58.bottom")}),1.0]])]});
            extrude(context, id + "F32", {"entities" : qUnion([Q0]), "operationType" : NewBodyOperationType.ADD, "depth" : 2.54 * mm, "offsetDistance" : 25.4 * mm});
        }
        {
            var Q0;
            Q0=makeQuery(id+"F5.boolean.opBoolean","MERGE",FACE,{"derivedFrom":[makeQuery(id+"F3.opExtrude","CAP_FACE",FACE,{"disambiguationData":[OSD([sQuery(id+"F2.wireOp",EDGE,"E1"),sQuery(id+"F2.wireOp",EDGE,"E2"),sQuery(id+"F2.wireOp",EDGE,"E3"),sQuery(id+"F2.wireOp",EDGE,"E4"),sQuery(id+"F2.wireOp",EDGE,"E5")])],"isStart":false}),makeQuery(id+"F5.opExtrude","SWEPT_FACE",FACE,{"disambiguationData":[OSD([sQuery(id+"F4.wireOp",EDGE,"E15")])]})]});
            var sketch = newSketch(context, id + "F33", { "sketchPlane" : qUnion([Q0])});
            skLineSegment(sketch, "E59", {"start": v(0, 2764.86) * mm, "end": v(-431.05, 2333.8) * mm});
            skLineSegment(sketch, "E60", {"start": v(-2764.86, 0) * mm, "end": v(0, 0) * mm});
            skLineSegment(sketch, "E61", {"start": v(0, 0) * mm, "end": v(0, 2764.86) * mm});
            skLineSegment(sketch, "E62", {"start": v(-431.05, 2333.8) * mm, "end": v(-431.05, 1724.2) * mm});
            skLineSegment(sketch, "E63", {"start": v(-431.05, 1724.2) * mm, "end": v(-1724.2, 431.05) * mm});
            skLineSegment(sketch, "E64", {"start": v(-1724.2, 431.05) * mm, "end": v(-2333.8, 431.05) * mm});
            skLineSegment(sketch, "E65.trimOffspring", {"start": v(-2333.8, 431.05) * mm, "end": v(-2764.86, 0) * mm});
            skSolve(sketch);
        }
        {
            var Q0;
            Q0 = qSketchRegion(id + "F33", true);
            extrude(context, id + "F34", {"entities" : qUnion([Q0]), "operationType" : NewBodyOperationType.REMOVE, "endBound" : BoundingType.THROUGH_ALL, "oppositeDirection" : true, "depth" : 25.4 * mm, "offsetDistance" : 25.4 * mm});
        }
        {
            var Q0;
            Q0=makeQuery(id+"F29.boolean.opBoolean","MERGE",FACE,{"derivedFrom":[makeQuery(id+"F5.opExtrude","SWEPT_FACE",FACE,{"disambiguationData":[OSD([sQuery(id+"F4.wireOp",EDGE,"E14")])]}),makeQuery(id+"F16.opShell","OFFSET_FACE",FACE,{"disambiguationData":[OSD([sQuery(id+"F2.wireOp",EDGE,"E1"),sQuery(id+"F2.wireOp",EDGE,"E2"),sQuery(id+"F2.wireOp",EDGE,"E3"),sQuery(id+"F2.wireOp",EDGE,"E4"),sQuery(id+"F2.wireOp",EDGE,"E5"),sQuery(id+"F4.wireOp",EDGE,"E15")])]}),makeQuery(id+"F29.opExtrude","SWEPT_FACE",FACE,{"disambiguationData":[OSD([sQuery(id+"F28.wireOp",EDGE,"E57.top")])]})]});
            var sketch = newSketch(context, id + "F35", { "sketchPlane" : qUnion([Q0])});
            skLineSegment(sketch, "E66.0", {"start": v(-634.25, -2417.98) * mm, "end": v(-203.2, -2849.03) * mm});
            skLineSegment(sketch, "E66.1", {"start": v(-2849.03, -203.2) * mm, "end": v(-2417.98, -634.25) * mm});
            skLineSegment(sketch, "E66.2", {"start": v(-2417.98, -634.25) * mm, "end": v(-1808.38, -634.25) * mm});
            skLineSegment(sketch, "E66.3", {"start": v(-1808.38, -634.25) * mm, "end": v(-634.25, -1808.38) * mm});
            skLineSegment(sketch, "E66.4", {"start": v(-634.25, -1808.38) * mm, "end": v(-634.25, -2417.98) * mm});
            skLineSegment(sketch, "E67", {"start": v(-2849.03, -203.2) * mm, "end": v(-2561.66, -203.2) * mm});
            skLineSegment(sketch, "E68", {"start": v(-2561.66, -203.2) * mm, "end": v(-2333.8, -431.05) * mm});
            skLineSegment(sketch, "E69", {"start": v(-2333.8, -431.05) * mm, "end": v(-1724.2, -431.05) * mm});
            skLineSegment(sketch, "E70", {"start": v(-1724.2, -431.05) * mm, "end": v(-431.05, -1724.2) * mm});
            skLineSegment(sketch, "E71", {"start": v(-431.05, -1724.2) * mm, "end": v(-431.05, -2333.8) * mm});
            skLineSegment(sketch, "E72", {"start": v(-431.05, -2333.8) * mm, "end": v(-203.2, -2561.66) * mm});
            skLineSegment(sketch, "E73", {"start": v(-203.2, -2561.66) * mm, "end": v(-203.2, -2849.03) * mm});
            skSolve(sketch);
        }
        {
            var Q0;
            Q0=makeQuery(id+"F35.imprint","IMPRINT",FACE,{"disambiguationData":[TD([[makeQuery(id+"F35.imprint","IMPRINT",EDGE,{"derivedFrom":sQuery(id+"F35.wireOp",EDGE,"E66.0")}),1.0]])]});
            var Q1;
            {var subQ2=sQuery(id+"F0.wireOp",EDGE,"E0.left");Q1=makeQuery(id+"F34.boolean.opBoolean","SPLIT",FACE,{"disambiguationData":[TD([makeQuery(id+"F1.opExtrude","SWEPT_FACE",FACE,{"disambiguationData":[OSD([subQ2])]})])],"derivedFrom":makeQuery(id+"F18.boolean.opBoolean","COPY",FACE,{"derivedFrom":makeQuery(id+"F18.opExtrude","SWEPT_FACE",FACE,{"disambiguationData":[OSD([sQuery(id+"F17.wireOp",EDGE,"E37.bottom")])]})})});}
            extrude(context, id + "F36", {"entities" : qUnion([Q0]), "operationType" : NewBodyOperationType.ADD, "endBound" : BoundingType.UP_TO_SURFACE, "depth" : 25.4 * mm, "endBoundEntityFace" : qUnion([Q1]), "offsetDistance" : 25.4 * mm});
        }
        {
            var Q0;
            Q0=makeQuery(id+"F16.opShell","OFFSET_FACE",FACE,{"disambiguationData":[OSD([sQuery(id+"F0.wireOp",EDGE,"E0.bottom")])]});
            var sketch = newSketch(context, id + "F37", { "sketchPlane" : qUnion([Q0])});
            skLineSegment(sketch, "E74", {"start": v(-2844.8, 3479.8) * mm, "end": v(-2540, 3479.8) * mm});
            skLineSegment(sketch, "E75", {"start": v(-2540, 3479.8) * mm, "end": v(-2540, 3302) * mm});
            skLineSegment(sketch, "E76", {"start": v(-2540, 3302) * mm, "end": v(-2235.2, 3302) * mm});
            skLineSegment(sketch, "E77", {"start": v(-2235.2, 3302) * mm, "end": v(-2235.2, 3124.2) * mm});
            skLineSegment(sketch, "E78", {"start": v(-2235.2, 3124.2) * mm, "end": v(-1930.4, 3124.2) * mm});
            skLineSegment(sketch, "E79", {"start": v(-1930.4, 3124.2) * mm, "end": v(-1930.4, 2946.4) * mm});
            skLineSegment(sketch, "E80", {"start": v(-1930.4, 2946.4) * mm, "end": v(-1625.6, 2946.4) * mm});
            skLineSegment(sketch, "E81", {"start": v(-1625.6, 2946.4) * mm, "end": v(-1625.6, 2768.6) * mm});
            skLineSegment(sketch, "E82", {"start": v(-1625.6, 2768.6) * mm, "end": v(-1320.8, 2768.6) * mm});
            skLineSegment(sketch, "E83", {"start": v(-1320.8, 2768.6) * mm, "end": v(-1320.8, 2590.8) * mm});
            skLineSegment(sketch, "E84", {"start": v(-2844.8, 3479.8) * mm, "end": v(-2844.8, 3454.4) * mm});
            skLineSegment(sketch, "E85", {"start": v(-2844.8, 3454.4) * mm, "end": v(-3106.06, 3454.4) * mm});
            skLineSegment(sketch, "E86", {"start": v(-3106.06, 3454.4) * mm, "end": v(-1016, 2235.2) * mm});
            skLineSegment(sketch, "E87", {"start": v(-2844.8, 3454.4) * mm, "end": v(-2844.8, 3302) * mm, "construction": true});
            skLineSegment(sketch, "E88", {"start": v(-2844.8, 3479.8) * mm, "end": v(-2540, 3302) * mm, "construction": true});
            skLineSegment(sketch, "E89", {"start": v(-1016, 2235.2) * mm, "end": v(-1320.8, 2235.2) * mm});
            skLineSegment(sketch, "E90", {"start": v(-1320.8, 2235.2) * mm, "end": v(-1320.8, 2057.4) * mm});
            skLineSegment(sketch, "E91", {"start": v(-1320.8, 2057.4) * mm, "end": v(-1625.6, 2057.4) * mm});
            skLineSegment(sketch, "E92", {"start": v(-1625.6, 2057.4) * mm, "end": v(-1625.6, 1879.6) * mm});
            skLineSegment(sketch, "E93", {"start": v(-1625.6, 1879.6) * mm, "end": v(-1930.4, 1879.6) * mm});
            skLineSegment(sketch, "E94", {"start": v(-1930.4, 1879.6) * mm, "end": v(-1930.4, 1701.8) * mm});
            skLineSegment(sketch, "E95", {"start": v(-1930.4, 1701.8) * mm, "end": v(-2235.2, 1701.8) * mm});
            skLineSegment(sketch, "E96", {"start": v(-2235.2, 1701.8) * mm, "end": v(-2235.2, 1524) * mm});
            skLineSegment(sketch, "E97", {"start": v(-2235.2, 1524) * mm, "end": v(-2540, 1524) * mm});
            skLineSegment(sketch, "E98", {"start": v(-2540, 1524) * mm, "end": v(-2540, 1346.2) * mm});
            skLineSegment(sketch, "E99", {"start": v(-2540, 1346.2) * mm, "end": v(-2844.8, 1346.2) * mm});
            skLineSegment(sketch, "E100", {"start": v(-2844.8, 1346.2) * mm, "end": v(-2844.8, 1168.4) * mm});
            skLineSegment(sketch, "E101", {"start": v(-2844.8, 1168.4) * mm, "end": v(-3149.6, 1168.4) * mm});
            skLineSegment(sketch, "E102", {"start": v(-3149.6, 1168.4) * mm, "end": v(-3149.6, 990.6) * mm});
            skLineSegment(sketch, "E103", {"start": v(-3149.6, 990.6) * mm, "end": v(-3454.4, 990.6) * mm});
            skLineSegment(sketch, "E104", {"start": v(-3454.4, 990.6) * mm, "end": v(-3454.4, 812.8) * mm});
            skLineSegment(sketch, "E105", {"start": v(-3454.4, 812.8) * mm, "end": v(-3759.2, 812.8) * mm});
            skLineSegment(sketch, "E106", {"start": v(-3759.2, 812.8) * mm, "end": v(-3759.2, 635) * mm});
            skLineSegment(sketch, "E107", {"start": v(-3759.2, 635) * mm, "end": v(-4064, 635) * mm});
            skLineSegment(sketch, "E108", {"start": v(-4064, 635) * mm, "end": v(-4064, 457.2) * mm});
            skLineSegment(sketch, "E109", {"start": v(-4064, 457.2) * mm, "end": v(-4368.8, 457.2) * mm});
            skLineSegment(sketch, "E110", {"start": v(-4368.8, 457.2) * mm, "end": v(-4368.8, 279.4) * mm});
            skLineSegment(sketch, "E111", {"start": v(-4368.8, 279.4) * mm, "end": v(-4673.6, 279.4) * mm});
            skLineSegment(sketch, "E112", {"start": v(-754.74, 2235.2) * mm, "end": v(-4238.17, 203.2) * mm});
            skLineSegment(sketch, "E113", {"start": v(-4238.17, 203.2) * mm, "end": v(-4673.6, 203.2) * mm});
            skLineSegment(sketch, "E114", {"start": v(-3149.6, 990.6) * mm, "end": v(-2844.8, 1168.4) * mm, "construction": true});
            skLineSegment(sketch, "E115", {"start": v(-1016, 2235.2) * mm, "end": v(-1016, 2082.8) * mm, "construction": true});
            skLineSegment(sketch, "E116", {"start": v(-1320.8, 2590.8) * mm, "end": v(-1016, 2590.8) * mm});
            skLineSegment(sketch, "E117", {"start": v(-1016, 2590.8) * mm, "end": v(-1016, 2413) * mm});
            skLineSegment(sketch, "E118", {"start": v(-1016, 2413) * mm, "end": v(-203.2, 2413) * mm});
            skLineSegment(sketch, "E119", {"start": v(-4673.6, 279.4) * mm, "end": v(-4673.6, 203.2) * mm});
            skLineSegment(sketch, "E120", {"start": v(-754.74, 2235.2) * mm, "end": v(-203.2, 2235.2) * mm});
            skLineSegment(sketch, "E121", {"start": v(-203.2, 2235.2) * mm, "end": v(-203.2, 2413) * mm});
            skSolve(sketch);
        }
        {
            var Q0;
            Q0=makeQuery(id+"F37.imprint","IMPRINT",FACE,{"disambiguationData":[TD([[makeQuery(id+"F37.imprint","IMPRINT",EDGE,{"derivedFrom":sQuery(id+"F37.wireOp",EDGE,"E74")}),-1.0]])]});
            extrude(context, id + "F38", {"entities" : qUnion([Q0]), "depth" : 1828.8 * mm, "offsetDistance" : 25.4 * mm});
        }
        {
            var Q0;
            Q0=makeQuery(id+"F38.opExtrude","SWEPT_FACE",FACE,{"disambiguationData":[OSD([sQuery(id+"F37.wireOp",EDGE,"E74")])]});
            var sketch = newSketch(context, id + "F39", { "sketchPlane" : qUnion([Q0])});
            skLineSegment(sketch, "E122.bottom", {"start": v(-3106.06, 4064) * mm, "end": v(-1016, 4064) * mm});
            skLineSegment(sketch, "E122.top", {"start": v(-3106.06, 4978.4) * mm, "end": v(-1016, 4978.4) * mm});
            skLineSegment(sketch, "E122.left", {"start": v(-3106.06, 4064) * mm, "end": v(-3106.06, 4978.4) * mm});
            skLineSegment(sketch, "E122.right", {"start": v(-1016, 4064) * mm, "end": v(-1016, 4978.4) * mm});
            skSolve(sketch);
        }
        {
            var Q0;
            Q0 = qSketchRegion(id + "F39", true);
            var Q1;
            Q1=makeQuery(id+"F38.opExtrude","SWEPT_FACE",FACE,{"disambiguationData":[OSD([sQuery(id+"F37.wireOp",EDGE,"E89")])]});
            extrude(context, id + "F40", {"entities" : qUnion([Q0]), "operationType" : NewBodyOperationType.REMOVE, "endBound" : BoundingType.UP_TO_SURFACE, "oppositeDirection" : true, "depth" : 25.4 * mm, "endBoundEntityFace" : qUnion([Q1]), "offsetDistance" : 25.4 * mm});
        }
        {
            var Q0;
            Q0=makeQuery(id+"F38.opExtrude","SWEPT_FACE",FACE,{"disambiguationData":[OSD([sQuery(id+"F37.wireOp",EDGE,"E120")])]});
            var sketch = newSketch(context, id + "F41", { "sketchPlane" : qUnion([Q0])});
            skLineSegment(sketch, "E123.bottom", {"start": v(-203.2, -5892.8) * mm, "end": v(-4673.6, -5892.8) * mm});
            skLineSegment(sketch, "E123.top", {"start": v(-203.2, -4978.4) * mm, "end": v(-4673.6, -4978.4) * mm});
            skLineSegment(sketch, "E123.left", {"start": v(-203.2, -5892.8) * mm, "end": v(-203.2, -4978.4) * mm});
            skLineSegment(sketch, "E123.right", {"start": v(-4673.6, -5892.8) * mm, "end": v(-4673.6, -4978.4) * mm});
            skSolve(sketch);
        }
        {
            var Q0;
            Q0 = qSketchRegion(id + "F41", true);
            var Q1;
            Q1=makeQuery(id+"F18.boolean.opBoolean","MERGE",FACE,{"derivedFrom":[makeQuery(id+"F16.opShell","OFFSET_FACE",FACE,{"disambiguationData":[OSD([sQuery(id+"F0.wireOp",EDGE,"E0.bottom"),sQuery(id+"F0.wireOp",EDGE,"E0.top"),sQuery(id+"F0.wireOp",EDGE,"E0.left"),sQuery(id+"F0.wireOp",EDGE,"E0.right")])]}),makeQuery(id+"F18.opExtrude","SWEPT_FACE",FACE,{"disambiguationData":[OSD([sQuery(id+"F17.wireOp",EDGE,"E37.top")])]})]});
            extrude(context, id + "F42", {"entities" : qUnion([Q0]), "operationType" : NewBodyOperationType.REMOVE, "endBound" : BoundingType.UP_TO_SURFACE, "depth" : 25.4 * mm, "endBoundEntityFace" : qUnion([Q1]), "offsetDistance" : 25.4 * mm});
        }
        {
            var Q0;
            Q0=makeQuery(id+"F29.boolean.opBoolean","MERGE",FACE,{"derivedFrom":[makeQuery(id+"F5.opExtrude","SWEPT_FACE",FACE,{"disambiguationData":[OSD([sQuery(id+"F4.wireOp",EDGE,"E14")])]}),makeQuery(id+"F16.opShell","OFFSET_FACE",FACE,{"disambiguationData":[OSD([sQuery(id+"F2.wireOp",EDGE,"E1"),sQuery(id+"F2.wireOp",EDGE,"E2"),sQuery(id+"F2.wireOp",EDGE,"E3"),sQuery(id+"F2.wireOp",EDGE,"E4"),sQuery(id+"F2.wireOp",EDGE,"E5"),sQuery(id+"F4.wireOp",EDGE,"E15")])]}),makeQuery(id+"F29.opExtrude","SWEPT_FACE",FACE,{"disambiguationData":[OSD([sQuery(id+"F28.wireOp",EDGE,"E57.top")])]})]});
            var sketch = newSketch(context, id + "F43", { "sketchPlane" : qUnion([Q0])});
            skLineSegment(sketch, "E124.0", {"start": v(-215.9, -15036.8) * mm, "end": v(-215.9, -2836.34) * mm});
            skLineSegment(sketch, "E124.1", {"start": v(-5283.2, -15036.8) * mm, "end": v(-215.9, -15036.8) * mm});
            skLineSegment(sketch, "E124.4", {"start": v(-5283.2, -215.9) * mm, "end": v(-5283.2, -15036.8) * mm});
            skLineSegment(sketch, "E124.5", {"start": v(-2836.34, -215.9) * mm, "end": v(-5283.2, -215.9) * mm});
            skLineSegment(sketch, "E125.0", {"start": v(-2417.98, -634.25) * mm, "end": v(-2836.34, -215.9) * mm});
            skLineSegment(sketch, "E125.1", {"start": v(-215.9, -2836.34) * mm, "end": v(-634.25, -2417.98) * mm});
            skLineSegment(sketch, "E125.2", {"start": v(-634.25, -2417.98) * mm, "end": v(-634.25, -1808.38) * mm});
            skLineSegment(sketch, "E125.3", {"start": v(-634.25, -1808.38) * mm, "end": v(-1808.38, -634.25) * mm});
            skLineSegment(sketch, "E125.4", {"start": v(-1808.38, -634.25) * mm, "end": v(-2417.98, -634.25) * mm});
            skSolve(sketch);
        }
        {
            var Q0;
            Q0 = qSketchRegion(id + "F43", true);
            extrude(context, id + "F44", {"entities" : qUnion([Q0]), "operationType" : NewBodyOperationType.REMOVE, "endBound" : BoundingType.UP_TO_NEXT, "oppositeDirection" : true, "depth" : 25.4 * mm, "offsetDistance" : 25.4 * mm});
        }
        {
            var Q0;
            Q0=makeQuery(id+"F5.boolean.opBoolean","MERGE",FACE,{"derivedFrom":[makeQuery(id+"F3.opExtrude","CAP_FACE",FACE,{"disambiguationData":[OSD([sQuery(id+"F2.wireOp",EDGE,"E1"),sQuery(id+"F2.wireOp",EDGE,"E2"),sQuery(id+"F2.wireOp",EDGE,"E3"),sQuery(id+"F2.wireOp",EDGE,"E4"),sQuery(id+"F2.wireOp",EDGE,"E5")])],"isStart":false}),makeQuery(id+"F5.opExtrude","SWEPT_FACE",FACE,{"disambiguationData":[OSD([sQuery(id+"F4.wireOp",EDGE,"E15")])]})]});
            var sketch = newSketch(context, id + "F45", { "sketchPlane" : qUnion([Q0])});
            skLineSegment(sketch, "E126", {"start": v(-215.9, 15036.8) * mm, "end": v(-5283.2, 215.9) * mm});
            skLineSegment(sketch, "E127", {"start": v(-5283.2, 215.9) * mm, "end": v(-5283.2, 215.9) * mm});
            skLineSegment(sketch, "E128", {"start": v(-5283.2, 215.9) * mm, "end": v(-5283.2, 15036.8) * mm});
            skLineSegment(sketch, "E129", {"start": v(-5283.2, 15036.8) * mm, "end": v(-215.9, 15036.8) * mm});
            skLineSegment(sketch, "E130", {"start": v(-215.9, 15036.8) * mm, "end": v(-215.9, 15036.8) * mm});
            skSolve(sketch);
        }
        {
            var Q0;
            Q0 = qSketchRegion(id + "F45", true);
            extrude(context, id + "F46", {"entities" : qUnion([Q0]), "oppositeDirection" : true, "depth" : 203.2 * mm, "offsetDistance" : 25.4 * mm});
        }
        {
            var Q0;
            {var subQ0=sQuery(id+"F2.wireOp",EDGE,"E3");var subQ3=sQuery(id+"F2.wireOp",EDGE,"E2");var subQ4=sQuery(id+"F2.wireOp",EDGE,"E4");var subQ5=sQuery(id+"F0.wireOp",EDGE,"E0.top");var subQ6=sQuery(id+"F0.wireOp",EDGE,"E0.bottom");var subQ7=sQuery(id+"F23.wireOp",EDGE,"E41");var subQ8=sQuery(id+"F2.wireOp",EDGE,"E5");var subQ9=sQuery(id+"F2.wireOp",EDGE,"E1");var subQ10=sQuery(id+"F0.wireOp",EDGE,"E0.left");var subQ11=sQuery(id+"F23.wireOp",EDGE,"E42");var subQ12=sQuery(id+"F23.wireOp",EDGE,"E43");Q0=makeQuery(id+"F32.boolean.opBoolean","SPLIT",FACE,{"disambiguationData":[TD([makeQuery(id+"F16.opShell","OFFSET_FACE",FACE,{"disambiguationData":[OSD([subQ6])]})])],"derivedFrom":makeQuery(id+"F29.boolean.opBoolean","MERGE",FACE,{"derivedFrom":[makeQuery(id+"F24.boolean.opBoolean","MERGE",FACE,{"derivedFrom":[makeQuery(id+"F15.boolean.opBoolean","MERGE",FACE,{"derivedFrom":[makeQuery(id+"F1.opExtrude","CAP_FACE",FACE,{"disambiguationData":[OSD([subQ6,subQ5,subQ10,sQuery(id+"F0.wireOp",EDGE,"E0.right")])],"isStart":false}),makeQuery(id+"F15.opExtrude","SWEPT_FACE",FACE,{"disambiguationData":[OSD([subQ0])]})]}),makeQuery(id+"F22.boolean.opBoolean","COPY",FACE,{"derivedFrom":makeQuery(id+"F22.opExtrude","CAP_FACE",FACE,{"disambiguationData":[OSD([subQ9,subQ3,subQ0,subQ4,subQ8])],"isStart":false})}),makeQuery(id+"F24.opExtrude","CAP_FACE",FACE,{"disambiguationData":[OSD([sQuery(id+"F23.wireOp",EDGE,"E40"),subQ7,subQ11,subQ12,sQuery(id+"F23.wireOp",EDGE,"E44")])],"isStart":true})]}),makeQuery(id+"F29.opExtrude","SWEPT_FACE",FACE,{"disambiguationData":[OSD([sQuery(id+"F28.wireOp",EDGE,"E57.bottom")])]})]})});}
            var sketch = newSketch(context, id + "F47", { "sketchPlane" : qUnion([Q0])});
            skLineSegment(sketch, "E131.bottom", {"start": v(-3309.58, 15036.8) * mm, "end": v(-1785.58, 15036.8) * mm});
            skLineSegment(sketch, "E131.top", {"start": v(-3309.58, 13004.8) * mm, "end": v(-1785.58, 13004.8) * mm});
            skLineSegment(sketch, "E131.left", {"start": v(-3309.58, 15036.8) * mm, "end": v(-3309.58, 13004.8) * mm});
            skLineSegment(sketch, "E131.right", {"start": v(-1785.58, 15036.8) * mm, "end": v(-1785.58, 13004.8) * mm});
            skLineSegment(sketch, "E132.bottom", {"start": v(-203.2, 6510.26) * mm, "end": v(-1117.6, 6510.26) * mm});
            skLineSegment(sketch, "E132.top", {"start": v(-203.2, 7424.66) * mm, "end": v(-1117.6, 7424.66) * mm});
            skLineSegment(sketch, "E132.left", {"start": v(-203.2, 6510.26) * mm, "end": v(-203.2, 7424.66) * mm});
            skLineSegment(sketch, "E132.right", {"start": v(-1117.6, 6510.26) * mm, "end": v(-1117.6, 7424.66) * mm});
            skLineSegment(sketch, "E133.bottom", {"start": v(-203.2, 7424.66) * mm, "end": v(-838.2, 7424.66) * mm});
            skLineSegment(sketch, "E133.top", {"start": v(-203.2, 10193.26) * mm, "end": v(-838.2, 10193.26) * mm});
            skLineSegment(sketch, "E133.left", {"start": v(-203.2, 7424.66) * mm, "end": v(-203.2, 10193.26) * mm});
            skLineSegment(sketch, "E133.right", {"start": v(-838.2, 7424.66) * mm, "end": v(-838.2, 10193.26) * mm});
            skLineSegment(sketch, "E134.bottom", {"start": v(-838.2, 10193.26) * mm, "end": v(-2626.83, 10193.26) * mm});
            skLineSegment(sketch, "E134.top", {"start": v(-838.2, 9558.26) * mm, "end": v(-2626.83, 9558.26) * mm});
            skLineSegment(sketch, "E134.left", {"start": v(-838.2, 10193.26) * mm, "end": v(-838.2, 9558.26) * mm});
            skLineSegment(sketch, "E134.right", {"start": v(-2626.83, 10193.26) * mm, "end": v(-2626.83, 9558.26) * mm});
            skLineSegment(sketch, "E135.bottom", {"start": v(-1752.6, 8643.86) * mm, "end": v(-2667, 8643.86) * mm});
            skLineSegment(sketch, "E135.top", {"start": v(-1752.6, 7424.66) * mm, "end": v(-2667, 7424.66) * mm});
            skLineSegment(sketch, "E135.left", {"start": v(-1752.6, 8643.86) * mm, "end": v(-1752.6, 7424.66) * mm});
            skLineSegment(sketch, "E135.right", {"start": v(-2667, 8643.86) * mm, "end": v(-2667, 7424.66) * mm});
            skLineSegment(sketch, "E136", {"start": v(-934.88, 15036.8) * mm, "end": v(-3982.88, 15036.8) * mm});
            skLineSegment(sketch, "E137", {"start": v(-934.88, 15036.8) * mm, "end": v(-934.88, 11684) * mm});
            skLineSegment(sketch, "E138", {"start": v(-934.88, 11684) * mm, "end": v(-3982.88, 11684) * mm});
            skLineSegment(sketch, "E139", {"start": v(-3982.88, 11684) * mm, "end": v(-3982.88, 15036.8) * mm});
            skSolve(sketch);
        }
        {
            var Q0;
            {var subQ0=sQuery(id+"F2.wireOp",EDGE,"E3");var subQ3=sQuery(id+"F2.wireOp",EDGE,"E2");var subQ4=sQuery(id+"F2.wireOp",EDGE,"E4");var subQ5=sQuery(id+"F0.wireOp",EDGE,"E0.top");var subQ6=sQuery(id+"F0.wireOp",EDGE,"E0.bottom");var subQ7=sQuery(id+"F23.wireOp",EDGE,"E41");var subQ8=sQuery(id+"F2.wireOp",EDGE,"E5");var subQ9=sQuery(id+"F2.wireOp",EDGE,"E1");var subQ10=sQuery(id+"F0.wireOp",EDGE,"E0.left");var subQ11=sQuery(id+"F23.wireOp",EDGE,"E42");var subQ12=sQuery(id+"F23.wireOp",EDGE,"E43");Q0=makeQuery(id+"F32.boolean.opBoolean","SPLIT",FACE,{"disambiguationData":[TD([makeQuery(id+"F16.opShell","OFFSET_FACE",FACE,{"disambiguationData":[OSD([subQ6])]})])],"derivedFrom":makeQuery(id+"F29.boolean.opBoolean","MERGE",FACE,{"derivedFrom":[makeQuery(id+"F24.boolean.opBoolean","MERGE",FACE,{"derivedFrom":[makeQuery(id+"F15.boolean.opBoolean","MERGE",FACE,{"derivedFrom":[makeQuery(id+"F1.opExtrude","CAP_FACE",FACE,{"disambiguationData":[OSD([subQ6,subQ5,subQ10,sQuery(id+"F0.wireOp",EDGE,"E0.right")])],"isStart":false}),makeQuery(id+"F15.opExtrude","SWEPT_FACE",FACE,{"disambiguationData":[OSD([subQ0])]})]}),makeQuery(id+"F22.boolean.opBoolean","COPY",FACE,{"derivedFrom":makeQuery(id+"F22.opExtrude","CAP_FACE",FACE,{"disambiguationData":[OSD([subQ9,subQ3,subQ0,subQ4,subQ8])],"isStart":false})}),makeQuery(id+"F24.opExtrude","CAP_FACE",FACE,{"disambiguationData":[OSD([sQuery(id+"F23.wireOp",EDGE,"E40"),subQ7,subQ11,subQ12,sQuery(id+"F23.wireOp",EDGE,"E44")])],"isStart":true})]}),makeQuery(id+"F29.opExtrude","SWEPT_FACE",FACE,{"disambiguationData":[OSD([sQuery(id+"F28.wireOp",EDGE,"E57.bottom")])]})]})});}
            var sketch = newSketch(context, id + "F48", { "sketchPlane" : qUnion([Q0])});
            skLineSegment(sketch, "E140.bottom", {"start": v(-203.2, 10058.4) * mm, "end": v(-1270, 10058.4) * mm});
            skLineSegment(sketch, "E140.top", {"start": v(-203.2, 11582.4) * mm, "end": v(-695.26, 11582.4) * mm});
            skLineSegment(sketch, "E140.left", {"start": v(-203.2, 10058.4) * mm, "end": v(-203.2, 11582.4) * mm});
            skLineSegment(sketch, "E140.right", {"start": v(-1270, 10058.4) * mm, "end": v(-1270, 11007.66) * mm});
            skLineSegment(sketch, "E141", {"start": v(-1270, 11007.66) * mm, "end": v(-695.26, 11582.4) * mm});
            skSolve(sketch);
        }
        {
            var Q0;
            Q0 = qSketchRegion(id + "F48", true);
            extrude(context, id + "F49", {"entities" : qUnion([Q0]), "depth" : 2438.4 * mm, "offsetDistance" : 25.4 * mm});
        }
    });
